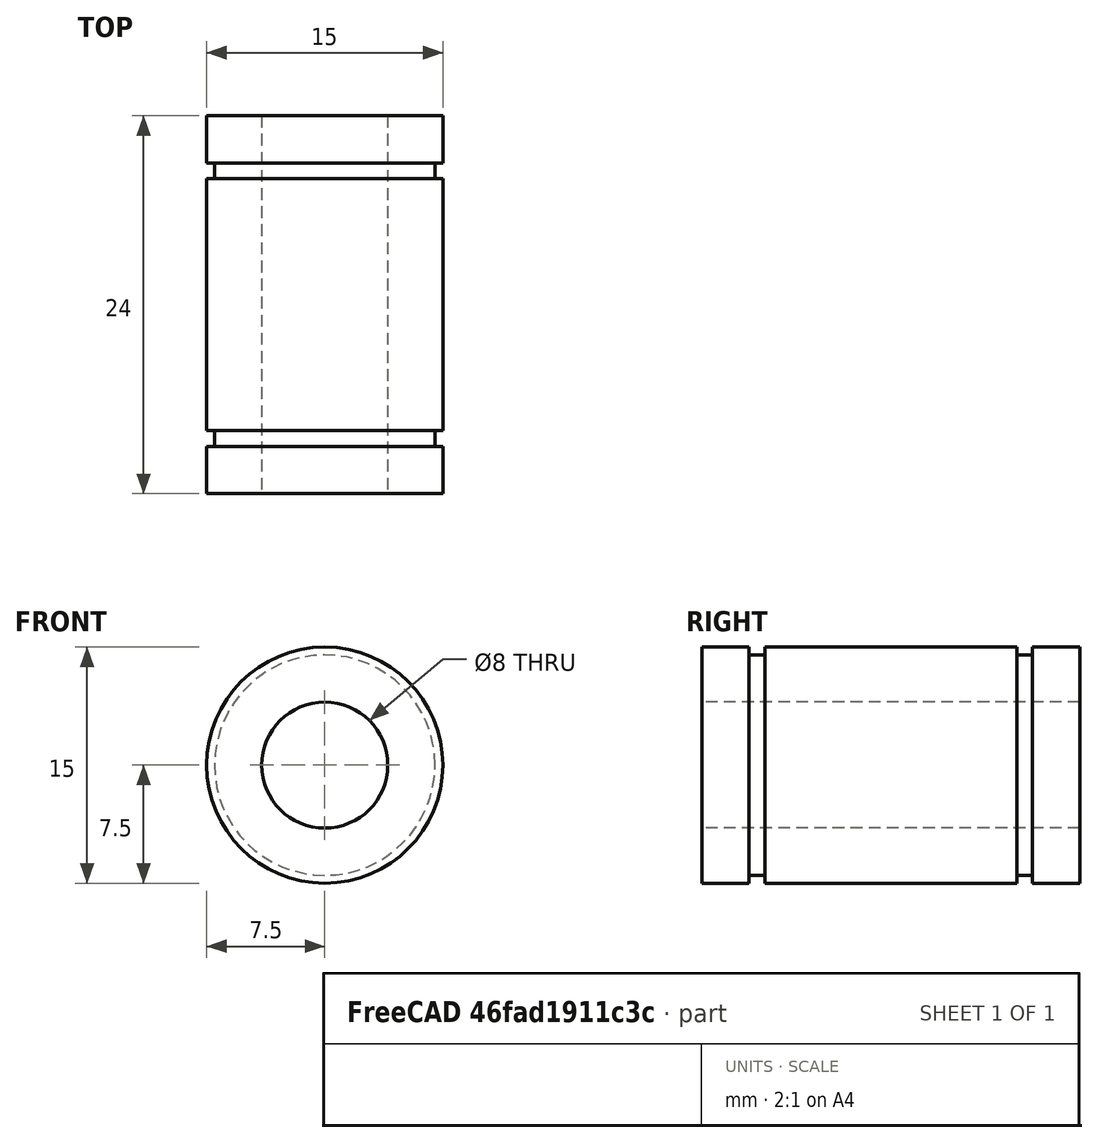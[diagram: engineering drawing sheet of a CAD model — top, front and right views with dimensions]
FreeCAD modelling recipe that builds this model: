
FCSTD DOCUMENT  (FreeCAD 0.19R22164 (Git))
Label: lm8uu_bearing
License: All rights reserved
LicenseURL: http://en.wikipedia.org/wiki/All_rights_reserved
objects: Sketcher::SketchObject×1, PartDesign::Revolution×1, PartDesign::Body×1
note: 4 computed .brp shape members not serialized (recipe doc carries the construction recipe); baked Part::Feature solids carry a one-line shape summary decoded from their .brp

FEATURE [Sketcher::SketchObject] Sketch
  MapMode = 5
  Support = -> [XY_Plane]
  sketch-geometry (12):
    g0: LineSegment StartX=-7.5 StartY=12 StartZ=0 EndX=-4 EndY=12 EndZ=0
    g1: LineSegment StartX=-4 StartY=-12 StartZ=0 EndX=-7.5 EndY=-12 EndZ=0
    g2: LineSegment StartX=-7.5 StartY=-12 StartZ=0 EndX=-7.5 EndY=-9 EndZ=0
    g3: LineSegment StartX=-4 StartY=12 StartZ=0 EndX=-4 EndY=-12 EndZ=0
    g4: LineSegment StartX=-7.5 StartY=9 StartZ=0 EndX=-7 EndY=9 EndZ=0
    g5: LineSegment StartX=-7 StartY=9 StartZ=0 EndX=-7 EndY=8 EndZ=0
    g6: LineSegment StartX=-7 StartY=8 StartZ=0 EndX=-7.5 EndY=8 EndZ=0
    g7: LineSegment StartX=-7.5 StartY=-8 StartZ=0 EndX=-7 EndY=-8 EndZ=0
    g8: LineSegment StartX=-7 StartY=-8 StartZ=0 EndX=-7 EndY=-9 EndZ=0
    g9: LineSegment StartX=-7 StartY=-9 StartZ=0 EndX=-7.5 EndY=-9 EndZ=0
    g10: LineSegment StartX=-7.5 StartY=9 StartZ=0 EndX=-7.5 EndY=12 EndZ=0
    g11: LineSegment StartX=-7.5 StartY=-8 StartZ=0 EndX=-7.5 EndY=8 EndZ=0
  constraints (33):
    c: Coincident(g1,g2)
    c: Coincident(g10,g0)
    c: Horizontal(g0)
    c: Horizontal(g1)
    c: Vertical(g2)
    c: DistanceY(g2,g10) = 24
    c: Vertical(g3)
    c: DistanceX(g0,g-1) = 7.5
    c: Coincident(g0,g3)
    c: Coincident(g1,g3)
    c: Coincident(g4,g5)
    c: Coincident(g5,g6)
    c: Horizontal(g4)
    c: Horizontal(g6)
    c: Vertical(g5)
    c: Coincident(g7,g8)
    c: Coincident(g8,g9)
    c: Horizontal(g7)
    c: Horizontal(g9)
    c: Vertical(g8)
    c: DistanceY(g8,g8) = 1
    c: DistanceY(g5,g5) = 1
    c: DistanceY(g1,g8) = 3
    c: DistanceY(g4,g0) = 3
    c: Coincident(g11,g6)
    c: Coincident(g10,g4)
    c: Tangent(g2,g10)
    c: Coincident(g2,g9)
    c: Coincident(g11,g7)
    c: Tangent(g2,g11)
    c: DistanceX(g9,g9) = 0.5
    c: DistanceX(g4,g4) = 0.5
    c: DistanceY(g1,g-1) = 12
FEATURE [PartDesign::Revolution] Revolution
  Angle = 360
  Axis = (0,1,0)
  Base = (0,0,0)
  Profile = -> Sketch
  ReferenceAxis = -> Sketch [V_Axis]
FEATURE [PartDesign::Body] Body
  Group = -> [Sketch,Revolution]
  Origin = -> Origin
  Tip = -> Revolution
